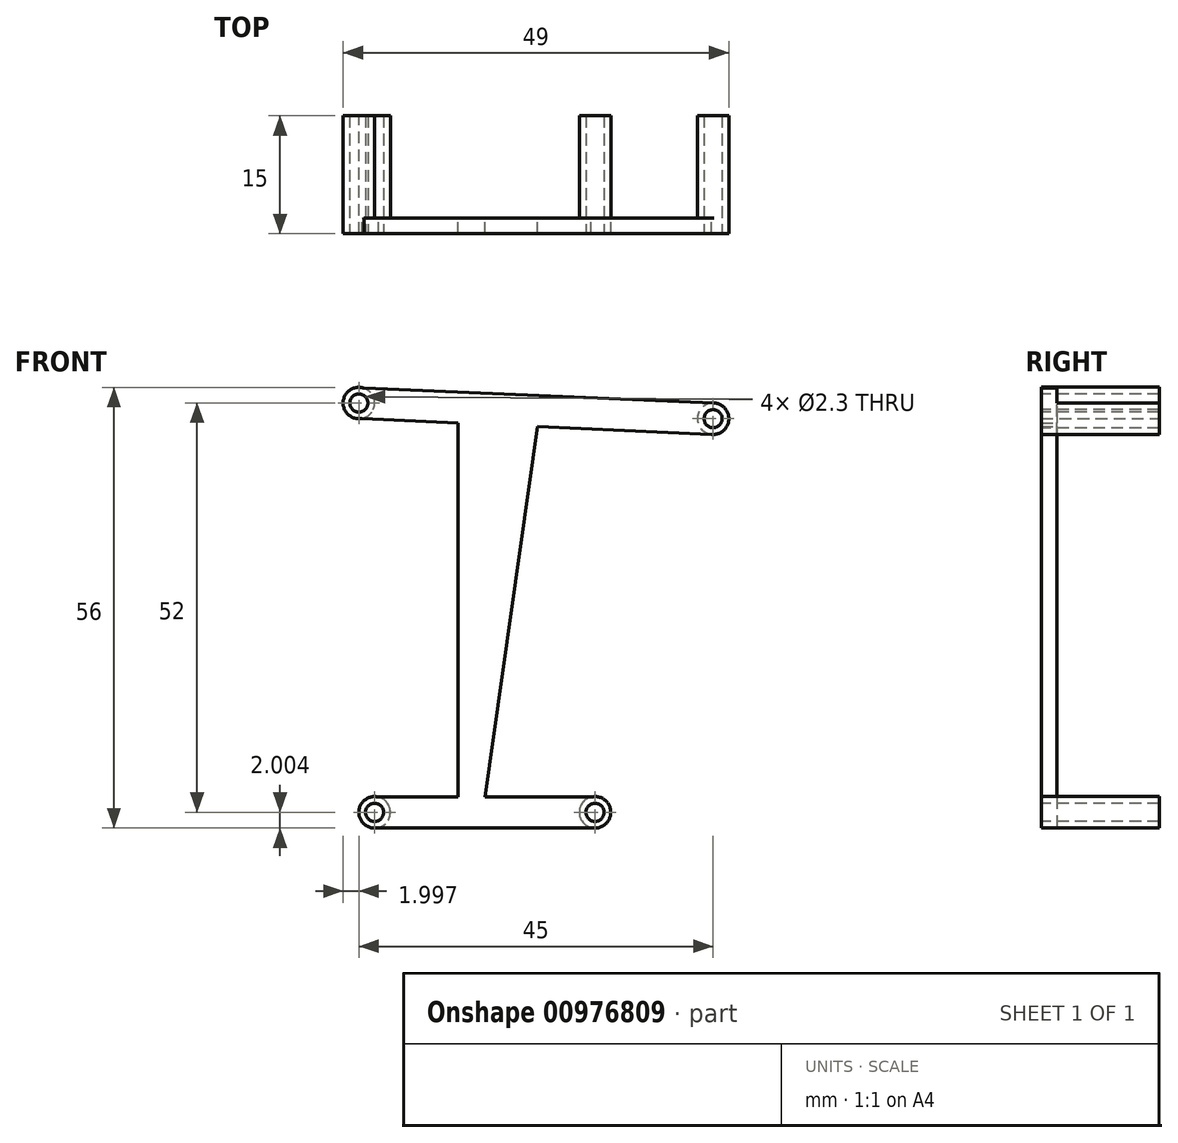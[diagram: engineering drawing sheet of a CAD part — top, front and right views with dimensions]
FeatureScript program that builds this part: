
annotation { "Feature Type Name" : "Feature", "Feature Type Description" : "" }
export const myFeature = defineFeature(function(context is Context, id is Id, definition is map)
    precondition{}
    {
        {
            var Q0;
            Q0=qCreatedBy(makeId("Front.planeOp"),FACE);
            var sketch = newSketch(context, id + "F0", { "sketchPlane" : qUnion([Q0])});
            skCircle(sketch, "E0", {"center": v(-41.74, -27.3) * mm, "radius": 2 * mm});
            skCircle(sketch, "E1", {"center": v(-13.74, -27.3) * mm, "radius": 2 * mm});
            skCircle(sketch, "E2", {"center": v(-43.74, 24.7) * mm, "radius": 2 * mm});
            skCircle(sketch, "E3", {"center": v(1.26, 22.7) * mm, "radius": 2 * mm});
            skLineSegment(sketch, "E4", {"start": v(-41.22, -25.37) * mm, "end": v(-14.26, -25.37) * mm});
            skLineSegment(sketch, "E5", {"start": v(-41.74, -29.3) * mm, "end": v(-13.74, -29.3) * mm});
            skLineSegment(sketch, "E6", {"start": v(-44.26, 26.63) * mm, "end": v(1.34, 24.7) * mm});
            skLineSegment(sketch, "E7", {"start": v(-43.35, 22.73) * mm, "end": v(1.26, 20.7) * mm});
            skLineSegment(sketch, "E8", {"start": v(-31.17, -25.37) * mm, "end": v(-31.17, 22.18) * mm});
            skLineSegment(sketch, "E9", {"start": v(-21.05, 21.71) * mm, "end": v(-27.74, -25.37) * mm});
            skSolve(sketch);
        }
        {
            var Q0;
            Q0 = qSketchRegion(id + "F0", true);
            extrude(context, id + "F1", {"entities" : qUnion([Q0]), "depth" : 15 * mm, "offsetDistance" : 25 * mm});
        }
        {
            var Q0;
            Q0=makeQuery(id+"F1.opExtrude","CAP_FACE",FACE,{"disambiguationData":[OSD([sQuery(id+"F0.wireOp",EDGE,"E0"),sQuery(id+"F0.wireOp",EDGE,"E1"),sQuery(id+"F0.wireOp",EDGE,"E2"),sQuery(id+"F0.wireOp",EDGE,"E3"),sQuery(id+"F0.wireOp",EDGE,"E4"),sQuery(id+"F0.wireOp",EDGE,"E5"),sQuery(id+"F0.wireOp",EDGE,"E6"),sQuery(id+"F0.wireOp",EDGE,"E7"),sQuery(id+"F0.wireOp",EDGE,"E8"),sQuery(id+"F0.wireOp",EDGE,"E9")])],"isStart":true});
            var sketch = newSketch(context, id + "F2", { "sketchPlane" : qUnion([Q0])});
            skArc(sketch, "E10", {"start": v(13.74, -29.3) * mm, "mid": v(15.73, -27.57) * mm, "end": v(14.26, -25.37) * mm});
            skArc(sketch, "E11", {"start": v(41.22, -25.37) * mm, "mid": v(39.76, -27.57) * mm, "end": v(41.74, -29.3) * mm});
            skArc(sketch, "E12", {"start": v(-1.07, 20.7) * mm, "mid": v(0.7, 23.07) * mm, "end": v(-1.81, 24.61) * mm});
            skLineSegment(sketch, "E13", {"start": v(-1.07, 20.7) * mm, "end": v(21.05, 21.71) * mm});
            skLineSegment(sketch, "E14", {"start": v(21.05, 21.71) * mm, "end": v(27.74, -25.37) * mm});
            skLineSegment(sketch, "E15", {"start": v(27.74, -25.37) * mm, "end": v(14.26, -25.37) * mm});
            skLineSegment(sketch, "E16", {"start": v(13.74, -29.3) * mm, "end": v(41.74, -29.3) * mm});
            skLineSegment(sketch, "E17", {"start": v(41.22, -25.37) * mm, "end": v(31.17, -25.37) * mm});
            skLineSegment(sketch, "E18", {"start": v(31.17, -25.37) * mm, "end": v(31.17, 22.18) * mm});
            skLineSegment(sketch, "E19", {"start": v(31.17, 22.18) * mm, "end": v(43.35, 22.73) * mm});
            skPoint(sketch, "E20.endSnap0", {"position": v(45.74, 24.84) * mm});
            skArc(sketch, "E21", {"start": v(43.07, 26.58) * mm, "mid": v(41.75, 24.55) * mm, "end": v(43.35, 22.73) * mm});
            skLineSegment(sketch, "E22", {"start": v(43.07, 26.58) * mm, "end": v(-1.34, 24.7) * mm});
            skSolve(sketch);
        }
        {
            var Q0;
            Q0 = qSketchRegion(id + "F2", true);
            extrude(context, id + "F3", {"entities" : qUnion([Q0]), "operationType" : NewBodyOperationType.REMOVE, "oppositeDirection" : true, "depth" : 13 * mm, "offsetDistance" : 25 * mm});
        }
        {
            var Q0;
            Q0=makeQuery(id+"F1.opExtrude","CAP_FACE",FACE,{"disambiguationData":[OSD([sQuery(id+"F0.wireOp",EDGE,"E0"),sQuery(id+"F0.wireOp",EDGE,"E1"),sQuery(id+"F0.wireOp",EDGE,"E2"),sQuery(id+"F0.wireOp",EDGE,"E3"),sQuery(id+"F0.wireOp",EDGE,"E4"),sQuery(id+"F0.wireOp",EDGE,"E5"),sQuery(id+"F0.wireOp",EDGE,"E6"),sQuery(id+"F0.wireOp",EDGE,"E7"),sQuery(id+"F0.wireOp",EDGE,"E8"),sQuery(id+"F0.wireOp",EDGE,"E9")])],"isStart":false});
            var sketch = newSketch(context, id + "F4", { "sketchPlane" : qUnion([Q0])});
            skCircle(sketch, "E23", {"center": v(-13.74, -27.3) * mm, "radius": 1.15 * mm});
            skCircle(sketch, "E24", {"center": v(-41.74, -27.3) * mm, "radius": 1.15 * mm});
            skCircle(sketch, "E25", {"center": v(1.26, 22.7) * mm, "radius": 1.15 * mm});
            skCircle(sketch, "E26", {"center": v(-43.74, 24.7) * mm, "radius": 1.15 * mm});
            skSolve(sketch);
        }
        {
            var Q0;
            Q0 = qSketchRegion(id + "F4", true);
            extrude(context, id + "F5", {"entities" : qUnion([Q0]), "operationType" : NewBodyOperationType.REMOVE, "oppositeDirection" : true, "depth" : 25 * mm, "offsetDistance" : 25 * mm});
        }
    });
